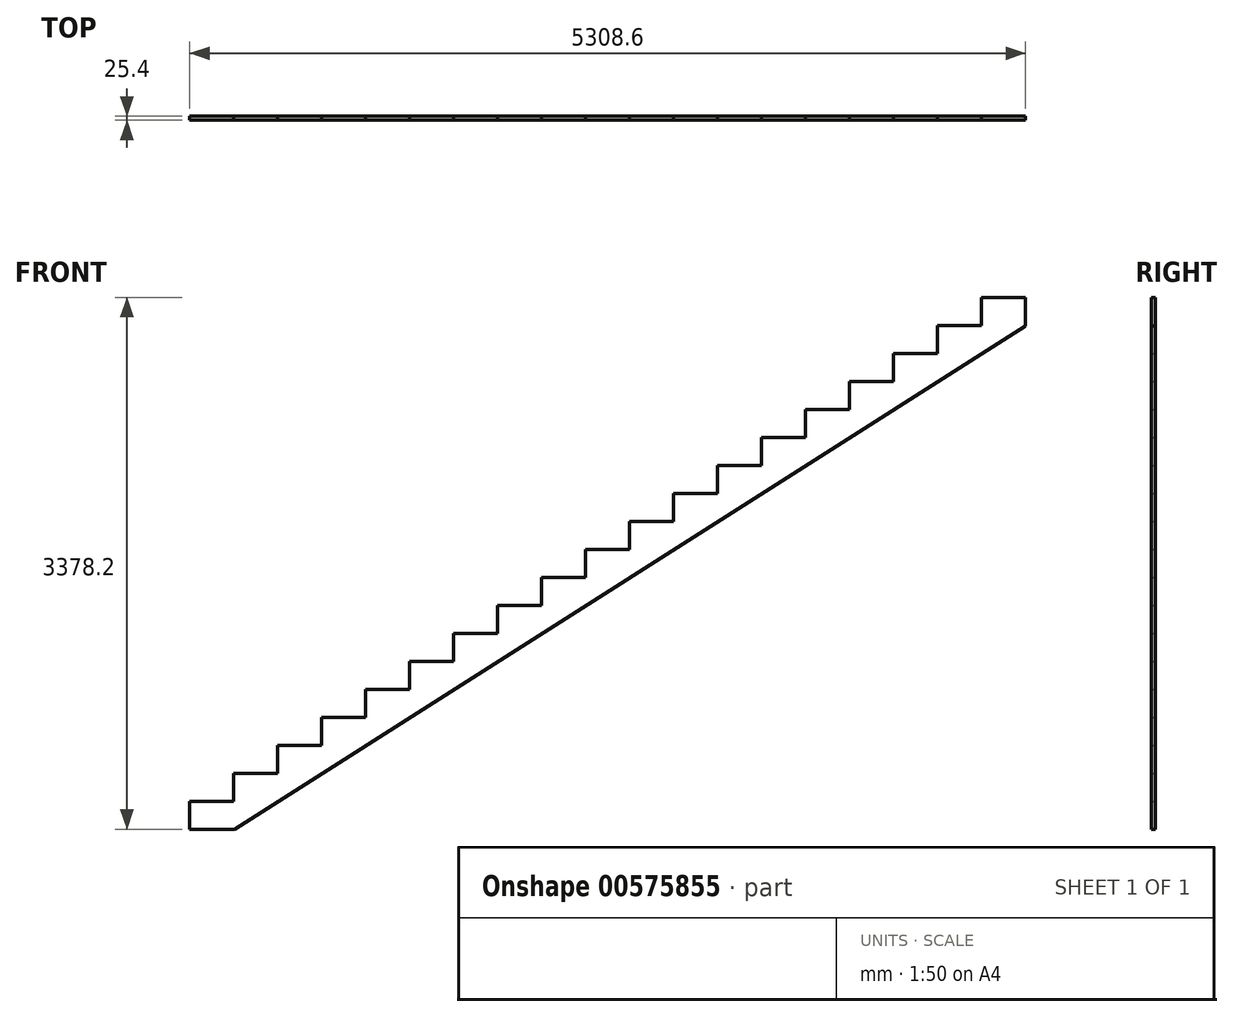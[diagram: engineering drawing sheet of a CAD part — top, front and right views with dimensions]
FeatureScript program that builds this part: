
annotation { "Feature Type Name" : "Feature", "Feature Type Description" : "" }
export const myFeature = defineFeature(function(context is Context, id is Id, definition is map)
    precondition{}
    {
        {
            var Q0;
            Q0=qCreatedBy(makeId("Front.planeOp"),FACE);
            var sketch = newSketch(context, id + "F0", { "sketchPlane" : qUnion([Q0])});
            skLineSegment(sketch, "E0", {"start": v(0, 0) * mm, "end": v(0, 177.8) * mm});
            skLineSegment(sketch, "E1", {"start": v(0, 177.8) * mm, "end": v(279.4, 177.8) * mm});
            skLineSegment(sketch, "E2", {"start": v(279.4, 177.8) * mm, "end": v(279.4, -2.84) * mm});
            skLineSegment(sketch, "E3", {"start": v(0, 0) * mm, "end": v(-279.4, 0) * mm});
            skLineSegment(sketch, "E4", {"start": v(-279.4, 0) * mm, "end": v(-279.4, -177.8) * mm});
            skLineSegment(sketch, "E5", {"start": v(-279.4, -177.8) * mm, "end": v(-558.8, -177.8) * mm});
            skLineSegment(sketch, "E6", {"start": v(-558.8, -177.8) * mm, "end": v(-558.8, -355.6) * mm});
            skLineSegment(sketch, "E7", {"start": v(-558.8, -355.6) * mm, "end": v(-838.2, -355.6) * mm});
            skLineSegment(sketch, "E8", {"start": v(-838.2, -355.6) * mm, "end": v(-838.2, -533.4) * mm});
            skLineSegment(sketch, "E9", {"start": v(-838.2, -533.4) * mm, "end": v(-1117.6, -533.4) * mm});
            skLineSegment(sketch, "E10", {"start": v(-1117.6, -533.4) * mm, "end": v(-1117.6, -711.2) * mm});
            skLineSegment(sketch, "E11", {"start": v(-1117.6, -711.2) * mm, "end": v(-1397, -711.2) * mm});
            skLineSegment(sketch, "E12", {"start": v(-1397, -711.2) * mm, "end": v(-1397, -889) * mm});
            skLineSegment(sketch, "E13", {"start": v(-1397, -889) * mm, "end": v(-1676.4, -889) * mm});
            skLineSegment(sketch, "E14", {"start": v(-1676.4, -889) * mm, "end": v(-1676.4, -1066.8) * mm});
            skLineSegment(sketch, "E15", {"start": v(-1676.4, -1066.8) * mm, "end": v(-1955.8, -1066.8) * mm});
            skLineSegment(sketch, "E16", {"start": v(-1955.8, -1066.8) * mm, "end": v(-1955.8, -1244.6) * mm});
            skLineSegment(sketch, "E17", {"start": v(-1955.8, -1244.6) * mm, "end": v(-2235.2, -1244.6) * mm});
            skLineSegment(sketch, "E18", {"start": v(-2235.2, -1244.6) * mm, "end": v(-2235.2, -1422.4) * mm});
            skLineSegment(sketch, "E19", {"start": v(-2235.2, -1422.4) * mm, "end": v(-2514.6, -1422.4) * mm});
            skLineSegment(sketch, "E20", {"start": v(-2514.6, -1422.4) * mm, "end": v(-2514.6, -1600.2) * mm});
            skLineSegment(sketch, "E21", {"start": v(-2514.6, -1600.2) * mm, "end": v(-2794, -1600.2) * mm});
            skLineSegment(sketch, "E22", {"start": v(-2794, -1600.2) * mm, "end": v(-2794, -1778) * mm});
            skLineSegment(sketch, "E23", {"start": v(-2794, -1778) * mm, "end": v(-3073.4, -1778) * mm});
            skLineSegment(sketch, "E24", {"start": v(-3073.4, -1778) * mm, "end": v(-3073.4, -1955.8) * mm});
            skLineSegment(sketch, "E25", {"start": v(-3073.4, -1955.8) * mm, "end": v(-3352.8, -1955.8) * mm});
            skLineSegment(sketch, "E26", {"start": v(-3352.8, -1955.8) * mm, "end": v(-3352.8, -2133.6) * mm});
            skLineSegment(sketch, "E27", {"start": v(-3352.8, -2133.6) * mm, "end": v(-3632.2, -2133.6) * mm});
            skLineSegment(sketch, "E28", {"start": v(-3632.2, -2133.6) * mm, "end": v(-3632.2, -2311.4) * mm});
            skLineSegment(sketch, "E29", {"start": v(-3632.2, -2311.4) * mm, "end": v(-3911.6, -2311.4) * mm});
            skLineSegment(sketch, "E30", {"start": v(-3911.6, -2311.4) * mm, "end": v(-3911.6, -2489.2) * mm});
            skLineSegment(sketch, "E31", {"start": v(-3911.6, -2489.2) * mm, "end": v(-4191, -2489.2) * mm});
            skLineSegment(sketch, "E32", {"start": v(-4191, -2667) * mm, "end": v(-4470.4, -2667) * mm});
            skLineSegment(sketch, "E33", {"start": v(-4470.4, -2667) * mm, "end": v(-4470.4, -2844.8) * mm});
            skLineSegment(sketch, "E34", {"start": v(-4470.4, -2844.8) * mm, "end": v(-4749.8, -2844.8) * mm});
            skLineSegment(sketch, "E35", {"start": v(-4749.8, -2844.8) * mm, "end": v(-4749.8, -3022.6) * mm});
            skLineSegment(sketch, "E36", {"start": v(-4749.8, -3022.6) * mm, "end": v(-5029.2, -3022.6) * mm});
            skLineSegment(sketch, "E37", {"start": v(-5029.2, -3022.6) * mm, "end": v(-5029.2, -3200.4) * mm});
            skLineSegment(sketch, "E38", {"start": v(-4191, -2489.2) * mm, "end": v(-4191, -2667) * mm});
            skLineSegment(sketch, "E39", {"start": v(-5029.2, -3200.4) * mm, "end": v(-4745.34, -3200.4) * mm});
            skLineSegment(sketch, "E40", {"start": v(279.4, -2.84) * mm, "end": v(-4745.34, -3200.4) * mm});
            skLineSegment(sketch, "E41", {"start": v(-4749.8, -3022.6) * mm, "end": v(0, 0) * mm, "construction": true});
            skSolve(sketch);
        }
        {
            var Q0;
            Q0 = qSketchRegion(id + "F0", true);
            extrude(context, id + "F1", {"entities" : qUnion([Q0]), "depth" : 25.4 * mm, "offsetDistance" : 25.4 * mm});
        }
    });
